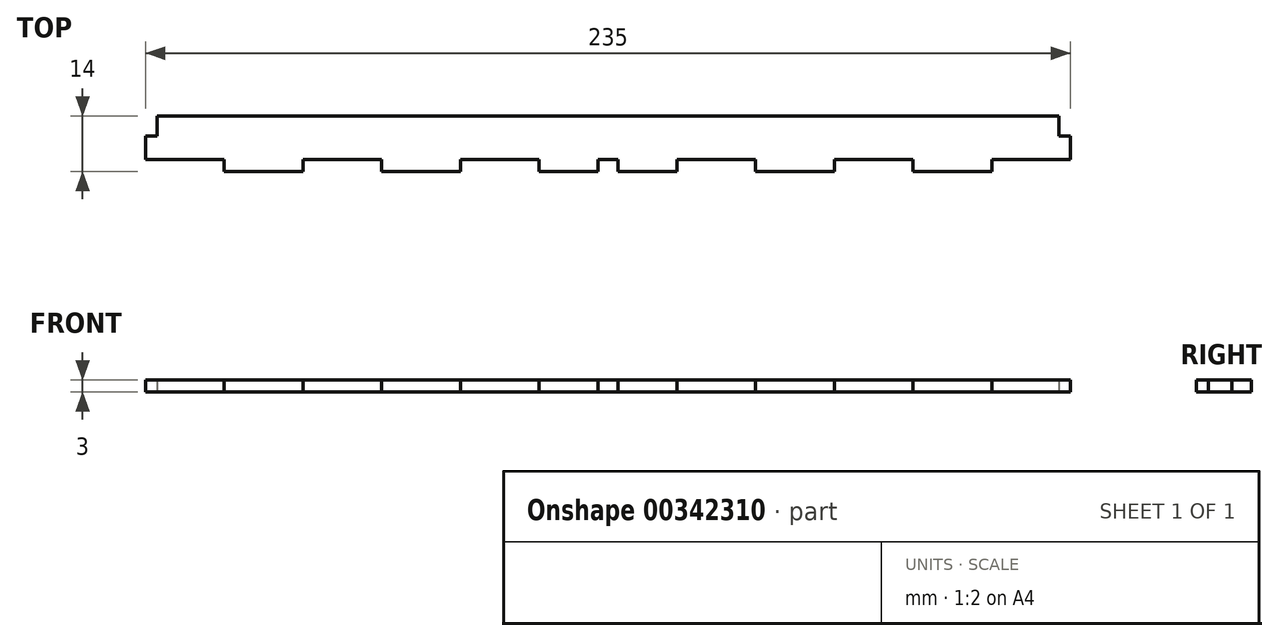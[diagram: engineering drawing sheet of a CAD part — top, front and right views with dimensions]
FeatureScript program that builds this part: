
annotation { "Feature Type Name" : "Feature", "Feature Type Description" : "" }
export const myFeature = defineFeature(function(context is Context, id is Id, definition is map)
    precondition{}
    {
        {
            var Q0;
            Q0=qCreatedBy(makeId("Top.planeOp"),FACE);
            var sketch = newSketch(context, id + "F0", { "sketchPlane" : qUnion([Q0])});
            skLineSegment(sketch, "E0", {"start": v(-117.5, -11) * mm, "end": v(-97.5, -11) * mm});
            skLineSegment(sketch, "E1", {"start": v(-97.5, -11) * mm, "end": v(-97.5, -14) * mm});
            skLineSegment(sketch, "E2", {"start": v(-97.5, -14) * mm, "end": v(-77.5, -14) * mm});
            skLineSegment(sketch, "E3", {"start": v(-77.5, -14) * mm, "end": v(-77.5, -11) * mm});
            skLineSegment(sketch, "E4", {"start": v(-77.5, -11) * mm, "end": v(-57.5, -11) * mm});
            skLineSegment(sketch, "E5", {"start": v(-57.5, -11) * mm, "end": v(-57.5, -14) * mm});
            skLineSegment(sketch, "E6", {"start": v(-57.5, -14) * mm, "end": v(-37.5, -14) * mm});
            skLineSegment(sketch, "E7", {"start": v(-37.5, -14) * mm, "end": v(-37.5, -11) * mm});
            skLineSegment(sketch, "E8", {"start": v(-37.5, -11) * mm, "end": v(-17.5, -11) * mm});
            skLineSegment(sketch, "E9", {"start": v(-17.5, -11) * mm, "end": v(-17.5, -14) * mm});
            skLineSegment(sketch, "E10", {"start": v(-17.5, -14) * mm, "end": v(-2.5, -14) * mm});
            skLineSegment(sketch, "E11", {"start": v(-2.5, -14) * mm, "end": v(-2.5, -11) * mm});
            skLineSegment(sketch, "E12", {"start": v(-2.5, -11) * mm, "end": v(2.5, -11) * mm});
            skLineSegment(sketch, "E13", {"start": v(2.5, -11) * mm, "end": v(2.5, -14) * mm});
            skLineSegment(sketch, "E14", {"start": v(2.5, -14) * mm, "end": v(17.5, -14) * mm});
            skLineSegment(sketch, "E15", {"start": v(17.5, -14) * mm, "end": v(17.5, -11) * mm});
            skLineSegment(sketch, "E16", {"start": v(17.5, -11) * mm, "end": v(37.5, -11) * mm});
            skLineSegment(sketch, "E17", {"start": v(37.5, -11) * mm, "end": v(37.5, -14) * mm});
            skLineSegment(sketch, "E18", {"start": v(37.5, -14) * mm, "end": v(57.5, -14) * mm});
            skLineSegment(sketch, "E19", {"start": v(57.5, -14) * mm, "end": v(57.5, -11) * mm});
            skLineSegment(sketch, "E20", {"start": v(57.5, -11) * mm, "end": v(77.5, -11) * mm});
            skLineSegment(sketch, "E21", {"start": v(77.5, -11) * mm, "end": v(77.5, -14) * mm});
            skLineSegment(sketch, "E22", {"start": v(77.5, -14) * mm, "end": v(97.5, -14) * mm});
            skLineSegment(sketch, "E23", {"start": v(97.5, -14) * mm, "end": v(97.5, -11) * mm});
            skLineSegment(sketch, "E24", {"start": v(97.5, -11) * mm, "end": v(117.5, -11) * mm});
            skLineSegment(sketch, "E25", {"start": v(-117.5, -11) * mm, "end": v(-117.5, -5) * mm});
            skLineSegment(sketch, "E26", {"start": v(-117.5, -5) * mm, "end": v(-114.5, -5) * mm});
            skLineSegment(sketch, "E27", {"start": v(-114.5, -5) * mm, "end": v(-114.5, 0) * mm});
            skLineSegment(sketch, "E28", {"start": v(117.5, -11) * mm, "end": v(117.5, -5) * mm});
            skLineSegment(sketch, "E29", {"start": v(117.5, -5) * mm, "end": v(114.5, -5) * mm});
            skLineSegment(sketch, "E30", {"start": v(114.5, -5) * mm, "end": v(114.5, 0) * mm});
            skLineSegment(sketch, "E31", {"start": v(-114.5, 0) * mm, "end": v(114.5, 0) * mm});
            skLineSegment(sketch, "E32", {"start": v(0, 0) * mm, "end": v(0, -11) * mm, "construction": true});
            skSolve(sketch);
        }
        {
            var Q0;
            Q0 = qSketchRegion(id + "F0", true);
            extrude(context, id + "F1", {"entities" : qUnion([Q0]), "offsetDistance" : 25 * mm, "depth" : 3 * mm});
        }
    });
